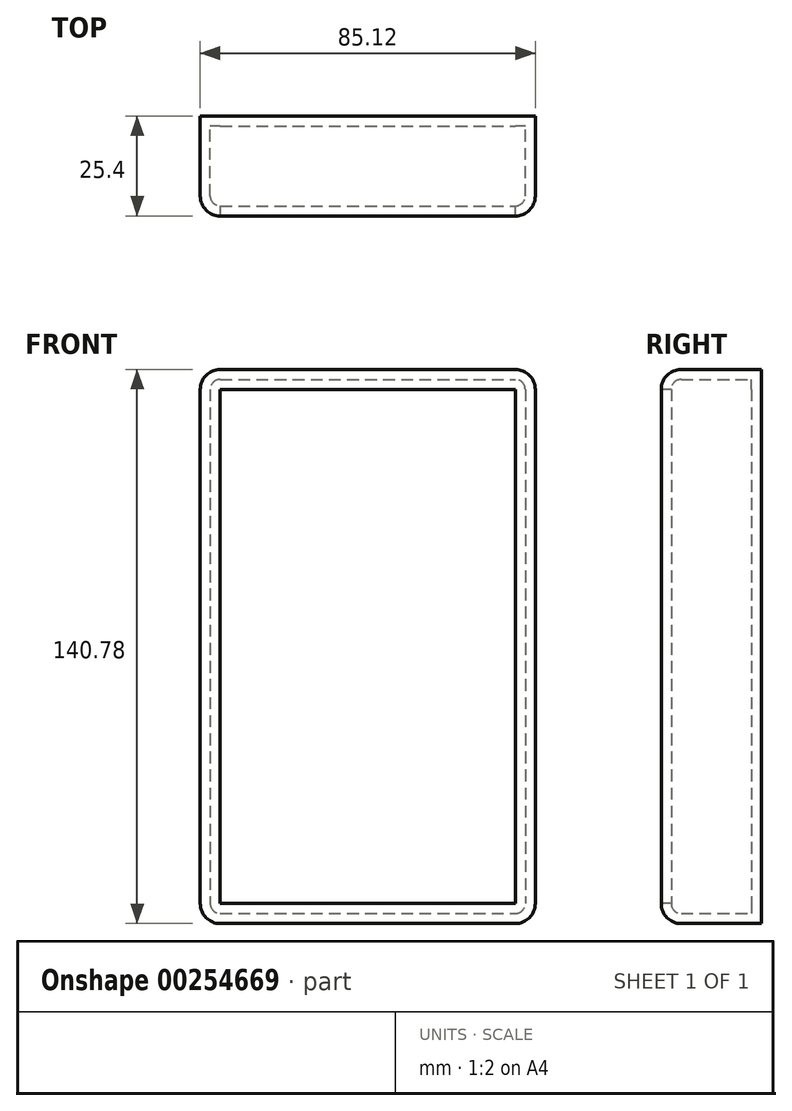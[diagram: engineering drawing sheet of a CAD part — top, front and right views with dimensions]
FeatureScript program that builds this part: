
annotation { "Feature Type Name" : "Feature", "Feature Type Description" : "" }
export const myFeature = defineFeature(function(context is Context, id is Id, definition is map)
    precondition{}
    {
        {
            var Q0;
            Q0=qCreatedBy(makeId("Front.planeOp"),FACE);
            var sketch = newSketch(context, id + "F0", { "sketchPlane" : qUnion([Q0])});
            skLineSegment(sketch, "E0.bottom", {"start": v(-42.56, 70.4) * mm, "end": v(42.56, 70.4) * mm});
            skLineSegment(sketch, "E0.top", {"start": v(-42.56, -70.4) * mm, "end": v(42.56, -70.4) * mm});
            skLineSegment(sketch, "E0.left", {"start": v(-42.56, 70.4) * mm, "end": v(-42.56, -70.4) * mm});
            skLineSegment(sketch, "E0.right", {"start": v(42.56, 70.4) * mm, "end": v(42.56, -70.4) * mm});
            skPoint(sketch, "E0.middle", {"position": v(0, 0) * mm});
            skSolve(sketch);
        }
        {
            var Q0;
            Q0=makeQuery(id+"F0.imprint","IMPRINT",FACE,{"disambiguationData":[TD([[makeQuery(id+"F0.imprint","IMPRINT",EDGE,{"derivedFrom":sQuery(id+"F0.wireOp",EDGE,"E0.bottom")}),-1.0]])]});
            extrude(context, id + "F1", {"entities" : qUnion([Q0]), "depth" : 25.4 * mm});
        }
        {
            var Q0;
            Q0=makeQuery(id+"F1.opExtrude","CAP_FACE",FACE,{"disambiguationData":[OSD([sQuery(id+"F0.wireOp",EDGE,"E0.bottom"),sQuery(id+"F0.wireOp",EDGE,"E0.top"),sQuery(id+"F0.wireOp",EDGE,"E0.left"),sQuery(id+"F0.wireOp",EDGE,"E0.right")])],"isStart":false});
            var Q1;
            Q1=makeQuery(id+"F1.opExtrude","SWEPT_EDGE",EDGE,{"disambiguationData":[OSD([sQuery(id+"F0.wireOp",EDGE,"E0.bottom"),sQuery(id+"F0.wireOp",EDGE,"E0.left")])]});
            var Q2;
            Q2=makeQuery(id+"F1.opExtrude","SWEPT_EDGE",EDGE,{"disambiguationData":[OSD([sQuery(id+"F0.wireOp",EDGE,"E0.bottom"),sQuery(id+"F0.wireOp",EDGE,"E0.right")])]});
            var Q3;
            Q3=makeQuery(id+"F1.opExtrude","SWEPT_EDGE",EDGE,{"disambiguationData":[OSD([sQuery(id+"F0.wireOp",EDGE,"E0.top"),sQuery(id+"F0.wireOp",EDGE,"E0.left")])]});
            var Q4;
            Q4=makeQuery(id+"F1.opExtrude","SWEPT_EDGE",EDGE,{"disambiguationData":[OSD([sQuery(id+"F0.wireOp",EDGE,"E0.top"),sQuery(id+"F0.wireOp",EDGE,"E0.right")])]});
            fillet(context, id + "F2", {"entities" : qUnion([Q0, Q1, Q2, Q3, Q4]), "radius" : 5.08 * mm, "tangentPropagation" : true, "allowEdgeOverflow" : false});
        }
        {
            var Q0;
            Q0=makeQuery(id+"F1.opExtrude","CAP_FACE",FACE,{"disambiguationData":[OSD([sQuery(id+"F0.wireOp",EDGE,"E0.bottom"),sQuery(id+"F0.wireOp",EDGE,"E0.top"),sQuery(id+"F0.wireOp",EDGE,"E0.left"),sQuery(id+"F0.wireOp",EDGE,"E0.right")])],"isStart":false});
            shell(context, id + "F3", {"entities" : qUnion([Q0]), "thickness" : 2.54 * mm});
        }
    });
